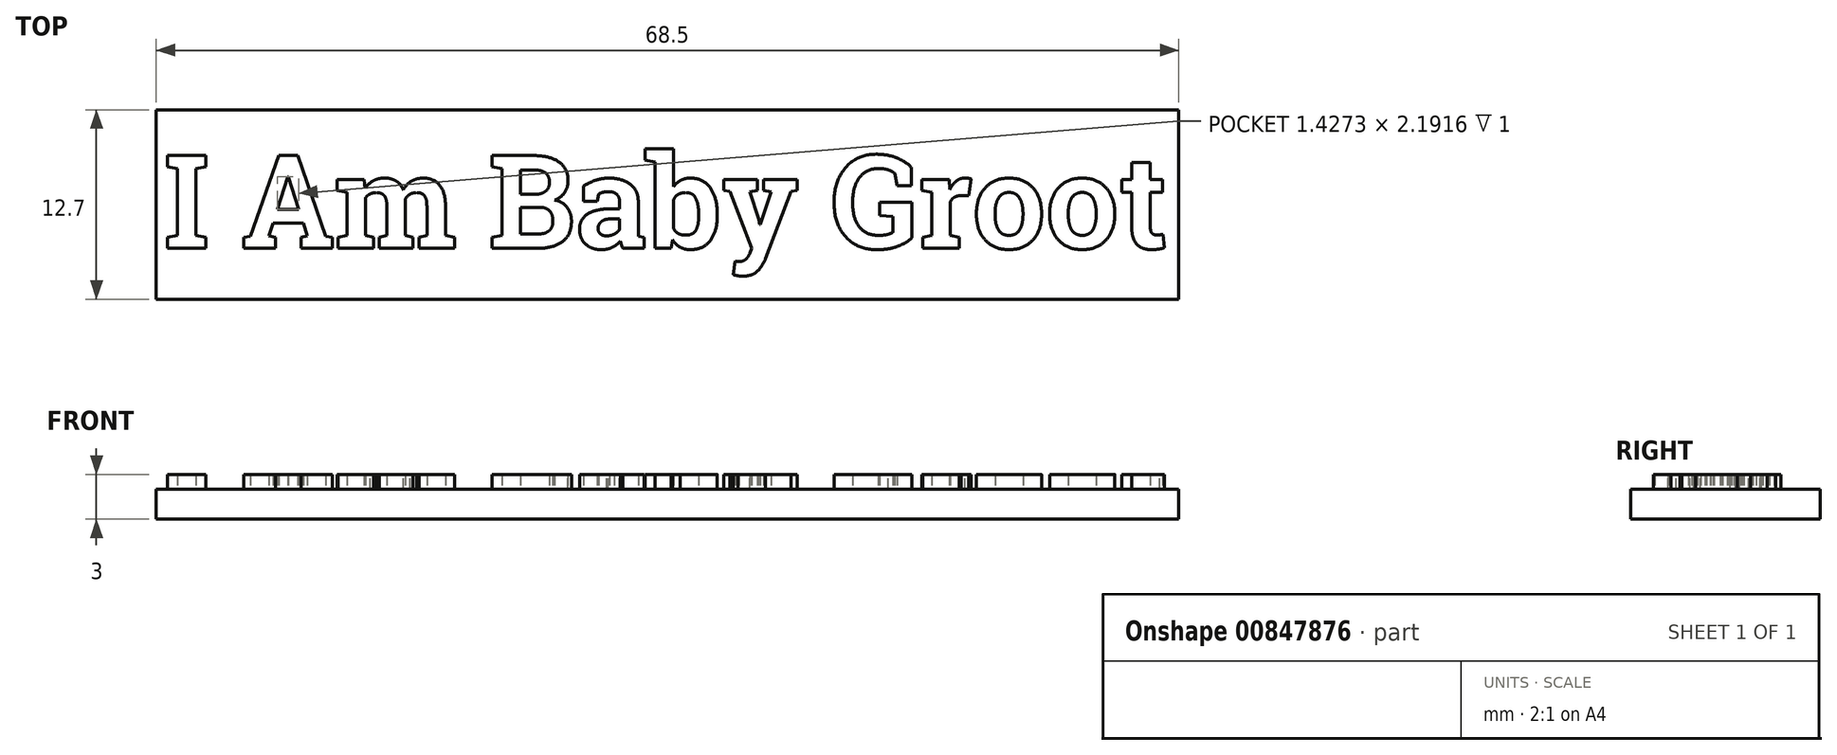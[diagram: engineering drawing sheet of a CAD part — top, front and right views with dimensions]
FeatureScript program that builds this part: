
annotation { "Feature Type Name" : "Feature", "Feature Type Description" : "" }
export const myFeature = defineFeature(function(context is Context, id is Id, definition is map)
    precondition{}
    {
        {
            var Q0;
            Q0=qCreatedBy(makeId("Top.planeOp"),FACE);
            var sketch = newSketch(context, id + "F0", { "sketchPlane" : qUnion([Q0])});
            skLineSegment(sketch, "E0.bottom", {"start": v(-32.18, 5.52) * mm, "end": v(36.32, 5.52) * mm});
            skLineSegment(sketch, "E0.top", {"start": v(-32.18, -7.18) * mm, "end": v(36.32, -7.18) * mm});
            skLineSegment(sketch, "E0.left", {"start": v(-32.18, 5.52) * mm, "end": v(-32.18, -7.18) * mm});
            skLineSegment(sketch, "E0.right", {"start": v(36.32, 5.52) * mm, "end": v(36.32, -7.18) * mm});
            skSolve(sketch);
        }
        {
            var Q0;
            Q0=makeQuery(id+"F0.imprint","IMPRINT",FACE,{"disambiguationData":[TD([[makeQuery(id+"F0.imprint","IMPRINT",EDGE,{"derivedFrom":sQuery(id+"F0.wireOp",EDGE,"E0.bottom")}),-1.0]])]});
            extrude(context, id + "F1", {"entities" : qUnion([Q0]), "depth" : 2 * mm, "offsetDistance" : 25 * mm});
        }
        {
            var Q0;
            Q0=makeQuery(id+"F1.opExtrude","CAP_FACE",FACE,{"disambiguationData":[OSD([sQuery(id+"F0.wireOp",EDGE,"E0.bottom"),sQuery(id+"F0.wireOp",EDGE,"E0.top"),sQuery(id+"F0.wireOp",EDGE,"E0.left"),sQuery(id+"F0.wireOp",EDGE,"E0.right")])],"isStart":false});
            var sketch = newSketch(context, id + "F2", { "sketchPlane" : qUnion([Q0])});
            skText(sketch, "E1", { "text": "I Am Baby Groot", "fontName": "RobotoSlab-Bold.ttf"});
            const initialGuessF2  = {"E1": [-0.03168, -0.00377, 1, 0, 0.0063]};
            skSetInitialGuess(sketch, initialGuessF2);
            skSolve(sketch);
        }
        {
            var Q0;
            Q0=qSketchRegion(id+"F2",true);
            extrude(context, id + "F3", {"entities" : qUnion([Q0]), "operationType" : NewBodyOperationType.ADD, "depth" : 1 * mm, "offsetDistance" : 25 * mm});
        }
    });
